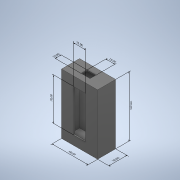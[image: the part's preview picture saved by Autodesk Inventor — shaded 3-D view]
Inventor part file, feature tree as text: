
AUTODESK INVENTOR PART (.ipt)
format: ipt  version: 2020 (Build 240168000, 168)  size: 163,328 bytes
history: native  units: mm
features: other x9, extrude x7, sketch x2
ambient origin geometry x8: Origin, YZ Plane, XZ Plane, XY Plane, X Axis, Y Axis, Z Axis, Center Point
bodies: Body1 (feature_tree)
feature tree (18):
  other  "Твердое тело1"
  other  "Аннотации"
  sketch  "Эскиз1"
  extrude  "Выдавливание1"  Depth=60.0mm
  extrude  "Выдавливание2"  Depth=100.0mm
  extrude  "Выдавливание3"  Depth=56.0mm
  extrude  "Выдавливание4"  Depth=96.0mm
  sketch  "Эскиз2"
  extrude  "Выдавливание5"  Depth=30.0mm TaperAngle=0.0deg
  extrude  "Выдавливание6"  Depth=28.0mm TaperAngle=0.0deg
  extrude  "Выдавливание9"  Depth=20.0mm
  other  "Линейный размер 1"
  other  "Линейный размер 2"
  other  "Линейный размер 3"
  other  "Линейный размер 4"
  other  "Линейный размер 5"
  other  "Линейный размер 6"
  other  "Линейный размер 7"
